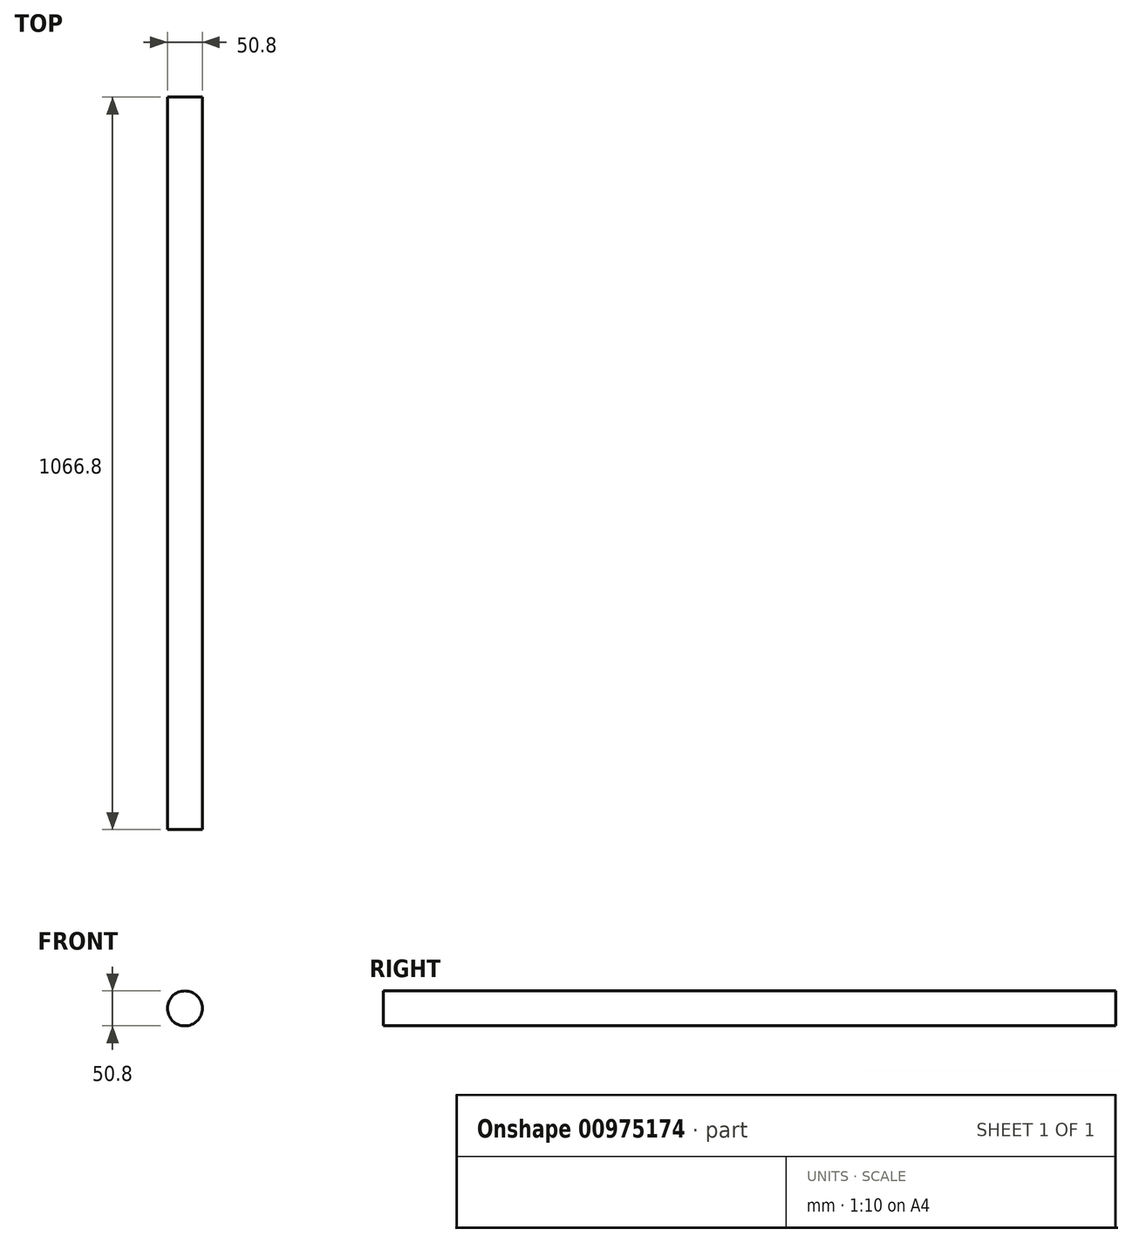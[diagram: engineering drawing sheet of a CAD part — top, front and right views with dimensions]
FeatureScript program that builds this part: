
annotation { "Feature Type Name" : "Feature", "Feature Type Description" : "" }
export const myFeature = defineFeature(function(context is Context, id is Id, definition is map)
    precondition{}
    {
        {
            var Q0;
            Q0=qCreatedBy(makeId("Front.planeOp"),FACE);
            var sketch = newSketch(context, id + "F0", { "sketchPlane" : qUnion([Q0])});
            skCircle(sketch, "E0", {"center": v(-44.05, 31.67) * mm, "radius": 25.4 * mm});
            skSolve(sketch);
        }
        {
            var Q0;
            Q0 = qSketchRegion(id + "F0", true);
            extrude(context, id + "F1", {"entities" : qUnion([Q0]), "depth" : 1066.8 * mm, "offsetDistance" : 25.4 * mm});
        }
    });
